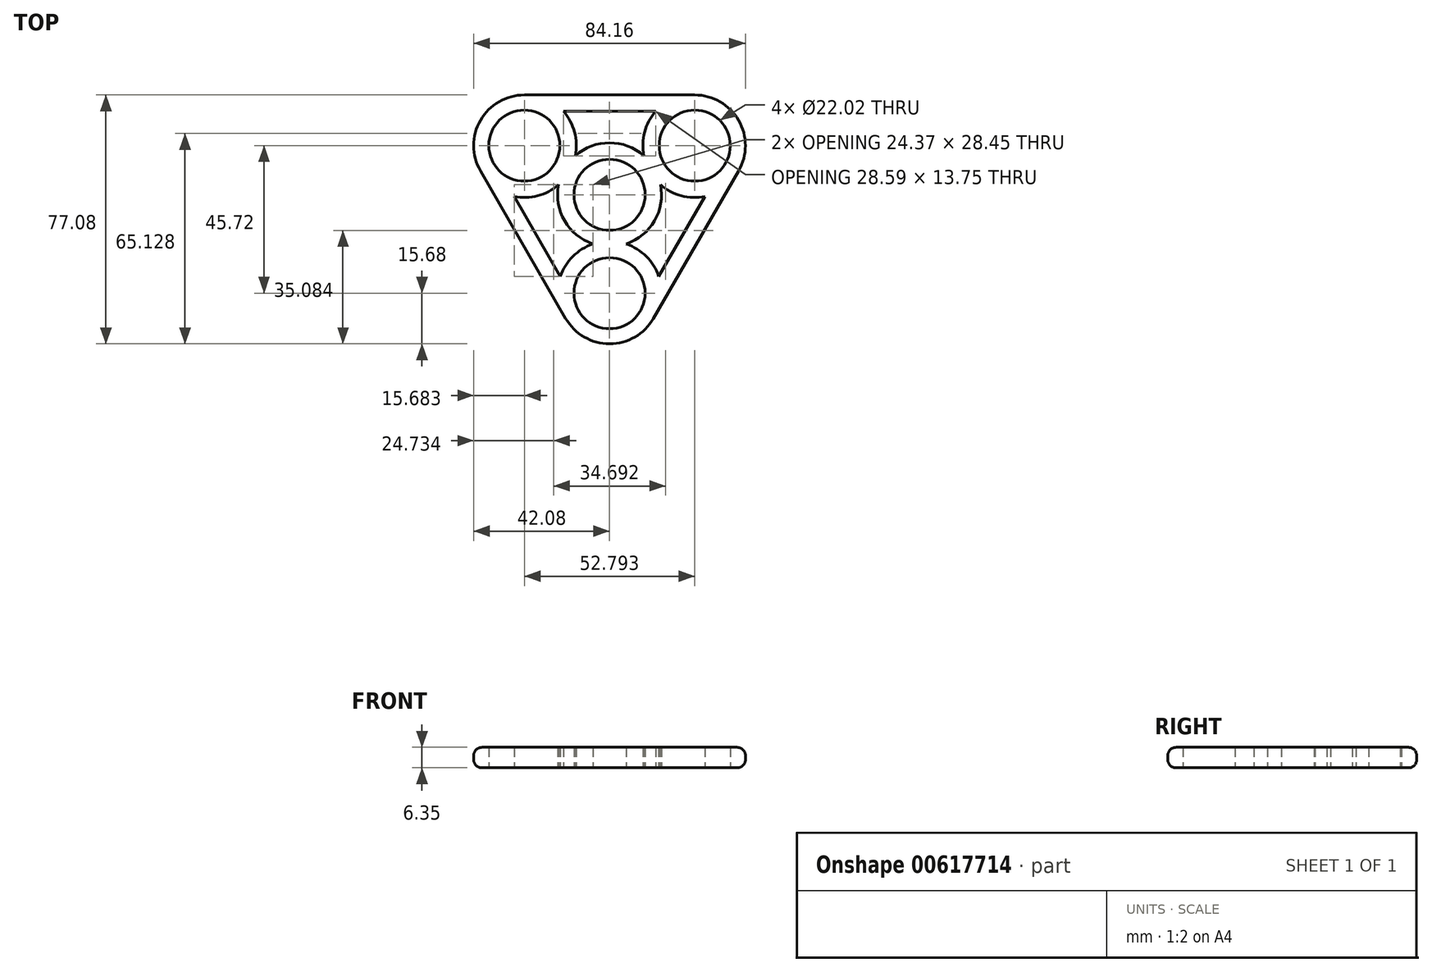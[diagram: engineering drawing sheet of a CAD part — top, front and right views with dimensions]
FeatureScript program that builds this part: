
annotation { "Feature Type Name" : "Feature", "Feature Type Description" : "" }
export const myFeature = defineFeature(function(context is Context, id is Id, definition is map)
    precondition{}
    {
        {
            var Q0;
            Q0=qCreatedBy(makeId("Top.planeOp"),FACE);
            var sketch = newSketch(context, id + "F0", { "sketchPlane" : qUnion([Q0])});
            skCircle(sketch, "E0", {"center": v(0, 0) * mm, "radius": 11.01 * mm});
            skLineSegment(sketch, "E1", {"start": v(0, 0) * mm, "end": v(26.4, 15.24) * mm});
            skLineSegment(sketch, "E2", {"start": v(0, 0) * mm, "end": v(0, -30.48) * mm});
            skLineSegment(sketch, "E3", {"start": v(0, 0) * mm, "end": v(-26.4, 15.24) * mm});
            skCircle(sketch, "E4", {"center": v(26.4, 15.24) * mm, "radius": 11.01 * mm});
            skCircle(sketch, "E5", {"center": v(0, -30.48) * mm, "radius": 11.01 * mm});
            skCircle(sketch, "E6", {"center": v(-26.4, 15.24) * mm, "radius": 11.01 * mm});
            skCircle(sketch, "E7", {"center": v(0, 0) * mm, "radius": 14.8 * mm});
            skCircle(sketch, "E8", {"center": v(26.4, 15.24) * mm, "radius": 15.68 * mm});
            skCircle(sketch, "E9", {"center": v(-26.4, 15.24) * mm, "radius": 15.68 * mm});
            skCircle(sketch, "E10", {"center": v(0, -30.48) * mm, "radius": 15.68 * mm});
            skLineSegment(sketch, "E11", {"start": v(-39.98, 7.4) * mm, "end": v(-13.58, -38.32) * mm});
            skLineSegment(sketch, "E12", {"start": v(39.98, 7.4) * mm, "end": v(13.58, -38.32) * mm});
            skLineSegment(sketch, "E13", {"start": v(-26.4, 30.92) * mm, "end": v(26.4, 30.92) * mm});
            skSolve(sketch);
        }
        {
            var Q0;
            Q0 = qSketchRegion(id + "F0", true);
            var Q1;
            {var subQ5=sQuery(id+"F0.wireOp",EDGE,"E3");var subQ6=sQuery(id+"F0.wireOp",EDGE,"E0");var subQ7=makeQuery(id+"F0.imprint","INTERSECT",VERTEX,{"derivedFrom":[subQ6,subQ5]});Q1=makeQuery(id+"F0.imprint","IMPRINT",FACE,{"disambiguationData":[TD([[makeQuery(id+"F0.imprint","IMPRINT",EDGE,{"disambiguationData":[TD([[subQ7,-1.0]])],"derivedFrom":subQ6}),-1.0]])]});}
            var Q2;
            {var subQ5=sQuery(id+"F0.wireOp",EDGE,"E1");var subQ6=sQuery(id+"F0.wireOp",EDGE,"E0");var subQ7=makeQuery(id+"F0.imprint","INTERSECT",VERTEX,{"derivedFrom":[subQ6,subQ5]});Q2=makeQuery(id+"F0.imprint","IMPRINT",FACE,{"disambiguationData":[TD([[makeQuery(id+"F0.imprint","IMPRINT",EDGE,{"disambiguationData":[TD([[subQ7,1.0]])],"derivedFrom":subQ6}),-1.0]])]});}
            var Q3;
            {var subQ6=sQuery(id+"F0.wireOp",EDGE,"E0");var subQ9=sQuery(id+"F0.wireOp",EDGE,"E3");var subQ10=makeQuery(id+"F0.imprint","INTERSECT",VERTEX,{"derivedFrom":[subQ6,subQ9]});Q3=makeQuery(id+"F0.imprint","IMPRINT",FACE,{"disambiguationData":[TD([[makeQuery(id+"F0.imprint","IMPRINT",EDGE,{"disambiguationData":[TD([[subQ10,1.0]])],"derivedFrom":subQ6}),-1.0]])]});}
            extrude(context, id + "F1", {"entities" : qUnion([Q0, Q1, Q2, Q3]), "depth" : 6.35 * mm, "offsetDistance" : 25.4 * mm});
        }
        {
            var Q0;
            Q0=makeQuery(id+"F1.opExtrude","CAP_EDGE",EDGE,{"disambiguationData":[OSD([sQuery(id+"F0.wireOp",EDGE,"2B1iHzSm-lQ5R-uiGI-lfUZ-LlhV3VTM2LeW")])],"isStart":false});
            var Q1;
            Q1=makeQuery(id+"F1.opExtrude","CAP_EDGE",EDGE,{"disambiguationData":[OSD([sQuery(id+"F0.wireOp",EDGE,"GPvWPNrS-pOYW-BTwK-Ex23-8gbyRmud1Gkm")])],"isStart":false});
            var Q2;
            Q2=makeQuery(id+"F1.opExtrude","CAP_EDGE",EDGE,{"disambiguationData":[OSD([sQuery(id+"F0.wireOp",EDGE,"B9QKughO-lUIP-PxLa-yllX-NnT0XOaiOLQM")])],"isStart":false});
            var Q3;
            Q3=makeQuery(id+"F1.opExtrude","CAP_EDGE",EDGE,{"disambiguationData":[OSD([sQuery(id+"F0.wireOp",EDGE,"E9")])],"isStart":false});
            var Q4;
            Q4=makeQuery(id+"F1.opExtrude","CAP_EDGE",EDGE,{"disambiguationData":[OSD([sQuery(id+"F0.wireOp",EDGE,"E10")])],"isStart":false});
            fillet(context, id + "F2", {"entities" : qUnion([Q0, Q1, Q2, Q3, Q4]), "radius" : 2.54 * mm, "tangentPropagation" : true, "allowEdgeOverflow" : false});
        }
        {
            var Q0;
            Q0=makeQuery(id+"F1.opExtrude","CAP_EDGE",EDGE,{"disambiguationData":[OSD([sQuery(id+"F0.wireOp",EDGE,"GPvWPNrS-pOYW-BTwK-Ex23-8gbyRmud1Gkm")])],"isStart":true});
            var Q1;
            Q1=makeQuery(id+"F1.opExtrude","CAP_EDGE",EDGE,{"disambiguationData":[OSD([sQuery(id+"F0.wireOp",EDGE,"E10")])],"isStart":true});
            var Q2;
            Q2=makeQuery(id+"F1.opExtrude","CAP_EDGE",EDGE,{"disambiguationData":[OSD([sQuery(id+"F0.wireOp",EDGE,"B9QKughO-lUIP-PxLa-yllX-NnT0XOaiOLQM")])],"isStart":true});
            var Q3;
            Q3=makeQuery(id+"F1.opExtrude","CAP_EDGE",EDGE,{"disambiguationData":[OSD([sQuery(id+"F0.wireOp",EDGE,"E8")])],"isStart":true});
            var Q4;
            Q4=makeQuery(id+"F1.opExtrude","CAP_EDGE",EDGE,{"disambiguationData":[OSD([sQuery(id+"F0.wireOp",EDGE,"E9")])],"isStart":true});
            fillet(context, id + "F3", {"entities" : qUnion([Q0, Q1, Q2, Q3, Q4]), "radius" : 2.54 * mm, "tangentPropagation" : true, "allowEdgeOverflow" : false});
        }
        {
            var Q0;
            Q0=makeQuery(id+"F1.opExtrude","CAP_FACE",FACE,{"disambiguationData":[OSD([sQuery(id+"F0.wireOp",EDGE,"E0"),sQuery(id+"F0.wireOp",EDGE,"E4"),sQuery(id+"F0.wireOp",EDGE,"E5"),sQuery(id+"F0.wireOp",EDGE,"E6"),sQuery(id+"F0.wireOp",EDGE,"E8"),sQuery(id+"F0.wireOp",EDGE,"E9"),sQuery(id+"F0.wireOp",EDGE,"E10"),sQuery(id+"F0.wireOp",EDGE,"E11"),sQuery(id+"F0.wireOp",EDGE,"E12"),sQuery(id+"F0.wireOp",EDGE,"E13")])],"isStart":false});
            var Q1;
            Q1=makeQuery(id+"F1.opExtrude","CAP_FACE",FACE,{"disambiguationData":[OSD([sQuery(id+"F0.wireOp",EDGE,"E0"),sQuery(id+"F0.wireOp",EDGE,"E4"),sQuery(id+"F0.wireOp",EDGE,"E5"),sQuery(id+"F0.wireOp",EDGE,"E6"),sQuery(id+"F0.wireOp",EDGE,"E8"),sQuery(id+"F0.wireOp",EDGE,"E9"),sQuery(id+"F0.wireOp",EDGE,"E10"),sQuery(id+"F0.wireOp",EDGE,"E11"),sQuery(id+"F0.wireOp",EDGE,"E12"),sQuery(id+"F0.wireOp",EDGE,"E13")])],"isStart":true});
            shell(context, id + "F4", {"entities" : qUnion([Q0, Q1]), "thickness" : 5.08 * mm});
        }
    });
